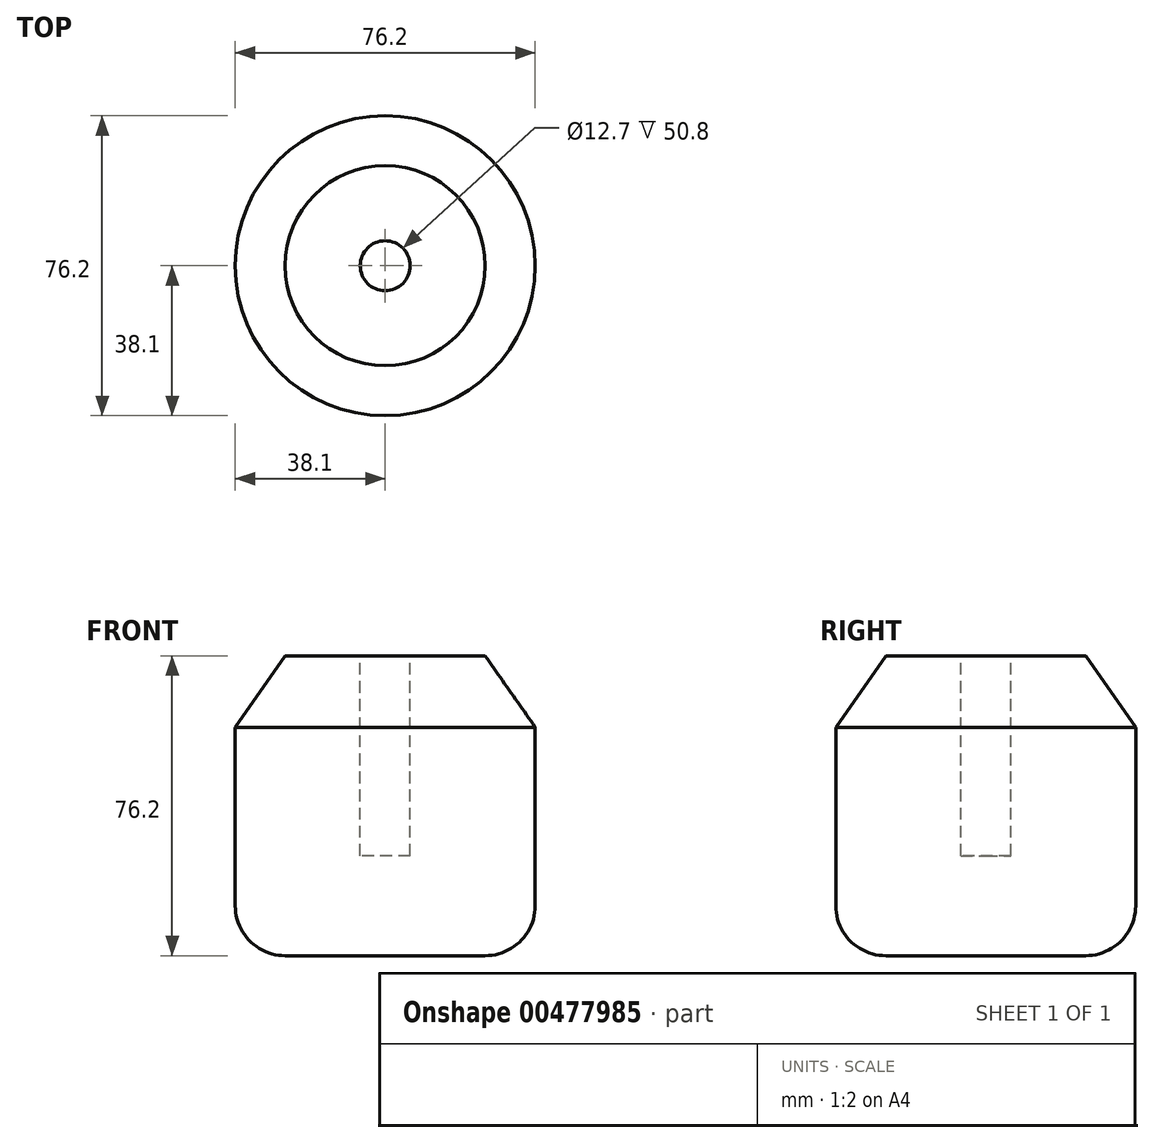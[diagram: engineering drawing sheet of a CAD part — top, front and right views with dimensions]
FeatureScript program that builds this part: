
annotation { "Feature Type Name" : "Feature", "Feature Type Description" : "" }
export const myFeature = defineFeature(function(context is Context, id is Id, definition is map)
    precondition{}
    {
        {
            var Q0;
            Q0=qCreatedBy(makeId("Top.planeOp"),FACE);
            var sketch = newSketch(context, id + "F0", { "sketchPlane" : qUnion([Q0])});
            skCircle(sketch, "E0", {"center": v(0, 0) * mm, "radius": 38.1 * mm});
            skSolve(sketch);
        }
        {
            var Q0;
            Q0=makeQuery(id+"F0.imprint","IMPRINT",FACE,{"disambiguationData":[TD([[makeQuery(id+"F0.imprint","IMPRINT",EDGE,{"derivedFrom":sQuery(id+"F0.wireOp",EDGE,"E0")}),1.0]])]});
            extrude(context, id + "F1", {"entities" : qUnion([Q0]), "depth" : 76.2 * mm});
        }
        {
            var Q0;
            Q0=makeQuery(id+"F1.opExtrude","CAP_EDGE",EDGE,{"disambiguationData":[OSD([sQuery(id+"F0.wireOp",EDGE,"E0")])],"isStart":true});
            fillet(context, id + "F2", {"entities" : qUnion([Q0]), "radius" : 12.7 * mm, "tangentPropagation" : true, "allowEdgeOverflow" : false});
        }
        {
            var Q0;
            Q0=makeQuery(id+"F1.opExtrude","CAP_FACE",FACE,{"disambiguationData":[OSD([sQuery(id+"F0.wireOp",EDGE,"E0")])],"isStart":false});
            var sketch = newSketch(context, id + "F3", { "sketchPlane" : qUnion([Q0])});
            skCircle(sketch, "E1", {"center": v(0, 0) * mm, "radius": 6.35 * mm});
            skSolve(sketch);
        }
        {
            var Q0;
            Q0=makeQuery(id+"F3.imprint","IMPRINT",FACE,{"disambiguationData":[TD([[makeQuery(id+"F3.imprint","IMPRINT",EDGE,{"derivedFrom":sQuery(id+"F3.wireOp",EDGE,"E1")}),1.0]])]});
            extrude(context, id + "F4", {"entities" : qUnion([Q0]), "operationType" : NewBodyOperationType.REMOVE, "oppositeDirection" : true, "depth" : 50.8 * mm});
        }
        {
            var Q0;
            Q0=makeQuery(id+"F1.opExtrude","CAP_EDGE",EDGE,{"disambiguationData":[OSD([sQuery(id+"F0.wireOp",EDGE,"E0")])],"isStart":false});
            chamfer(context, id + "F5", {"entities" : qUnion([Q0]), "chamferType" : ChamferType.OFFSET_ANGLE, "width" : 12.7 * mm, "oppositeDirection" : false, "angle" : 55 * degree, "tangentPropagation" : true});
        }
    });
